# Revit family: Handshower-American_Standard-FloWise_Modern-1660_Series
name_source: partatom
category: Plumbing Fixtures
revit_build: Autodesk Revit 2015 (Build: 20140606_1530(x64)
units: mm (PartAtom-declared; Revit-internal decimal feet)

## types (2) — shared parameters
Assembly Code = D2010700
CW Connection = Yes
CWFU = 3
Default Elevation = 0"
Description = Flowise Modern Water Saving Hand Shower
Flow Rate = 1.5gpm
HW Connection = Yes
HWFU = 3
Height = 9 1/2"
Manufacturer = American Standard
NPT Connection Size = 1/2"
Price = Prices may vary. Please consult Manufacturer Representative for most up-to-date price list.
Product Documentation Link = https://www.americanstandard-us.com
Product Page URL = https://www.americanstandard-us.com
URL = https://www.americanstandard-us.com
Vent Connection = No
WFU = 4
Waste Connection = Yes
Width = 2 1/2"

## per-type parameters (varying)
| type | Finish | Material |
| 1660.641.002 | Brass-American Standard-002-Polished Chrome | Brass-American Standard-002-Polished Chrome |
| 1660.641.295 | Brass-American Standard-295-Brushed Nickel | Brass-American Standard-295-Brushed Nickel |

note: column(s) folded — value = type name in every type: Model

## geometry (parser evidence)
native form markers: Sweep x2
no freeform markers — native parametric forms only
